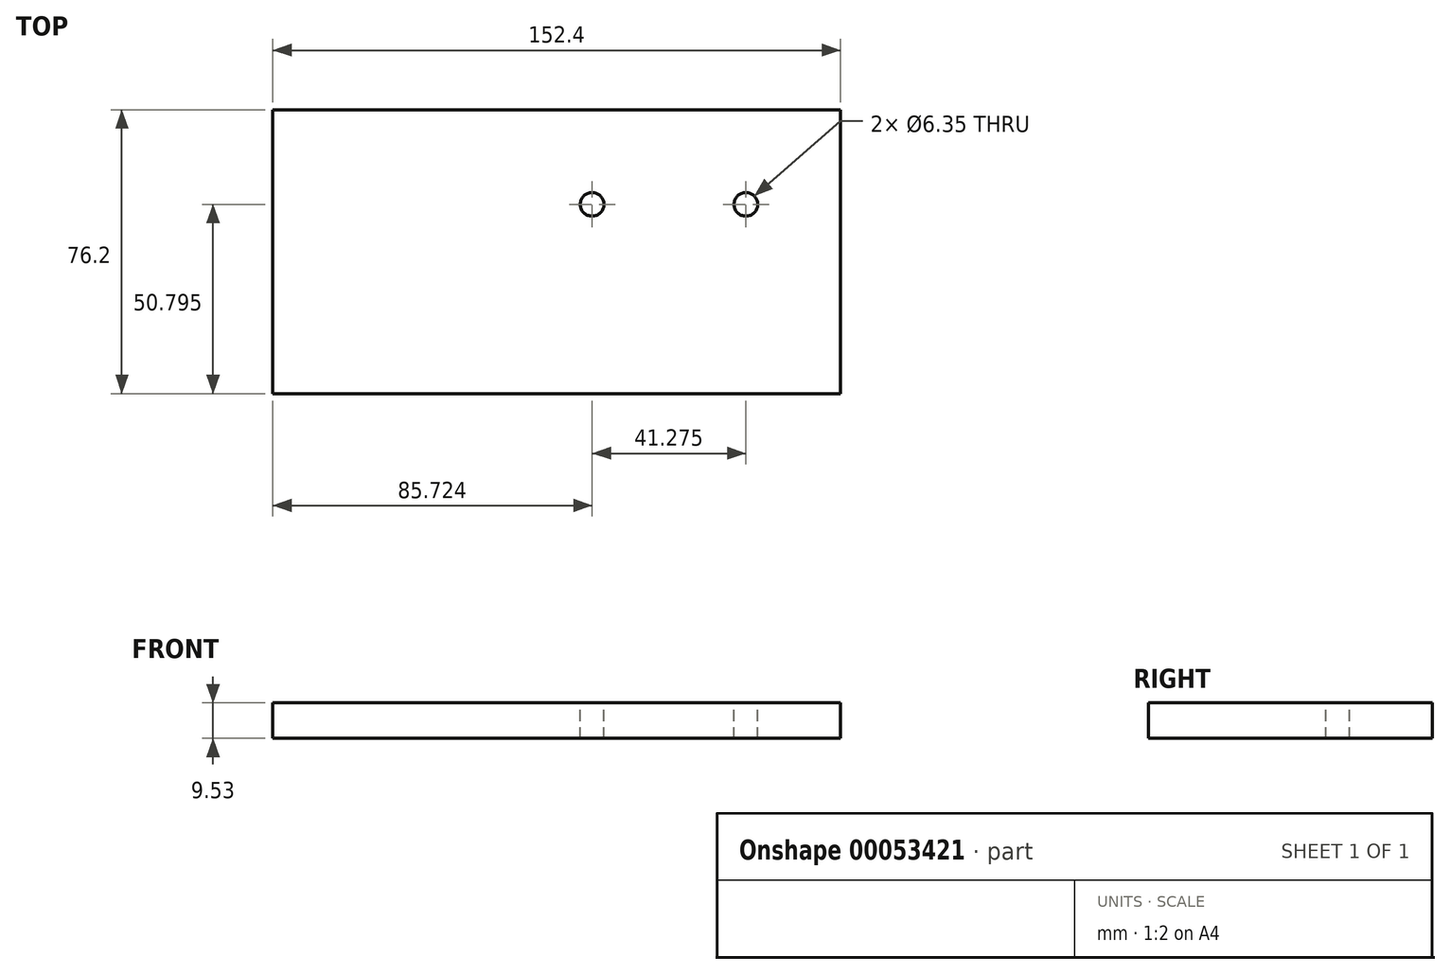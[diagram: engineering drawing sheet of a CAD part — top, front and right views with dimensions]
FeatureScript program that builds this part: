
annotation { "Feature Type Name" : "Feature", "Feature Type Description" : "" }
export const myFeature = defineFeature(function(context is Context, id is Id, definition is map)
    precondition{}
    {
        {
            var Q0;
            Q0=qCreatedBy(makeId("Top.planeOp"),FACE);
            var sketch = newSketch(context, id + "F0", { "sketchPlane" : qUnion([Q0])});
            skLineSegment(sketch, "E0.bottom", {"start": v(-148.5, -2.73) * mm, "end": v(3.9, -2.73) * mm});
            skLineSegment(sketch, "E0.top", {"start": v(-148.5, -78.93) * mm, "end": v(3.9, -78.93) * mm});
            skLineSegment(sketch, "E0.left", {"start": v(-148.5, -2.73) * mm, "end": v(-148.5, -78.93) * mm});
            skLineSegment(sketch, "E0.right", {"start": v(3.9, -2.73) * mm, "end": v(3.9, -78.93) * mm});
            skSolve(sketch);
        }
        {
            var Q0;
            Q0 = qSketchRegion(id + "F0", true);
            extrude(context, id + "F1", {"entities" : qUnion([Q0]), "depth" : 9.52 * mm});
        }
        {
            var Q0;
            Q0=makeQuery(id+"F1.opExtrude","CAP_FACE",FACE,{"disambiguationData":[OSD([sQuery(id+"F0.wireOp",EDGE,"E0.bottom"),sQuery(id+"F0.wireOp",EDGE,"E0.top"),sQuery(id+"F0.wireOp",EDGE,"E0.left"),sQuery(id+"F0.wireOp",EDGE,"E0.right")])],"isStart":false});
            var sketch = newSketch(context, id + "F2", { "sketchPlane" : qUnion([Q0])});
            skCircle(sketch, "E1", {"center": v(-21.5, -28.13) * mm, "radius": 3.17 * mm});
            skSolve(sketch);
        }
        {
            var Q0;
            Q0 = qSketchRegion(id + "F2", true);
            extrude(context, id + "F3", {"entities" : qUnion([Q0]), "operationType" : NewBodyOperationType.REMOVE, "oppositeDirection" : true, "depth" : 25.4 * mm});
        }
        {
            var Q0;
            Q0=makeQuery(id+"F1.opExtrude","CAP_FACE",FACE,{"disambiguationData":[OSD([sQuery(id+"F0.wireOp",EDGE,"E0.bottom"),sQuery(id+"F0.wireOp",EDGE,"E0.top"),sQuery(id+"F0.wireOp",EDGE,"E0.left"),sQuery(id+"F0.wireOp",EDGE,"E0.right")])],"isStart":false});
            var sketch = newSketch(context, id + "F4", { "sketchPlane" : qUnion([Q0])});
            skCircle(sketch, "E2", {"center": v(-62.77, -28.13) * mm, "radius": 3.18 * mm});
            skSolve(sketch);
        }
        {
            var Q0;
            Q0 = qSketchRegion(id + "F4", true);
            extrude(context, id + "F5", {"entities" : qUnion([Q0]), "operationType" : NewBodyOperationType.REMOVE, "oppositeDirection" : true, "depth" : 25.4 * mm});
        }
    });
